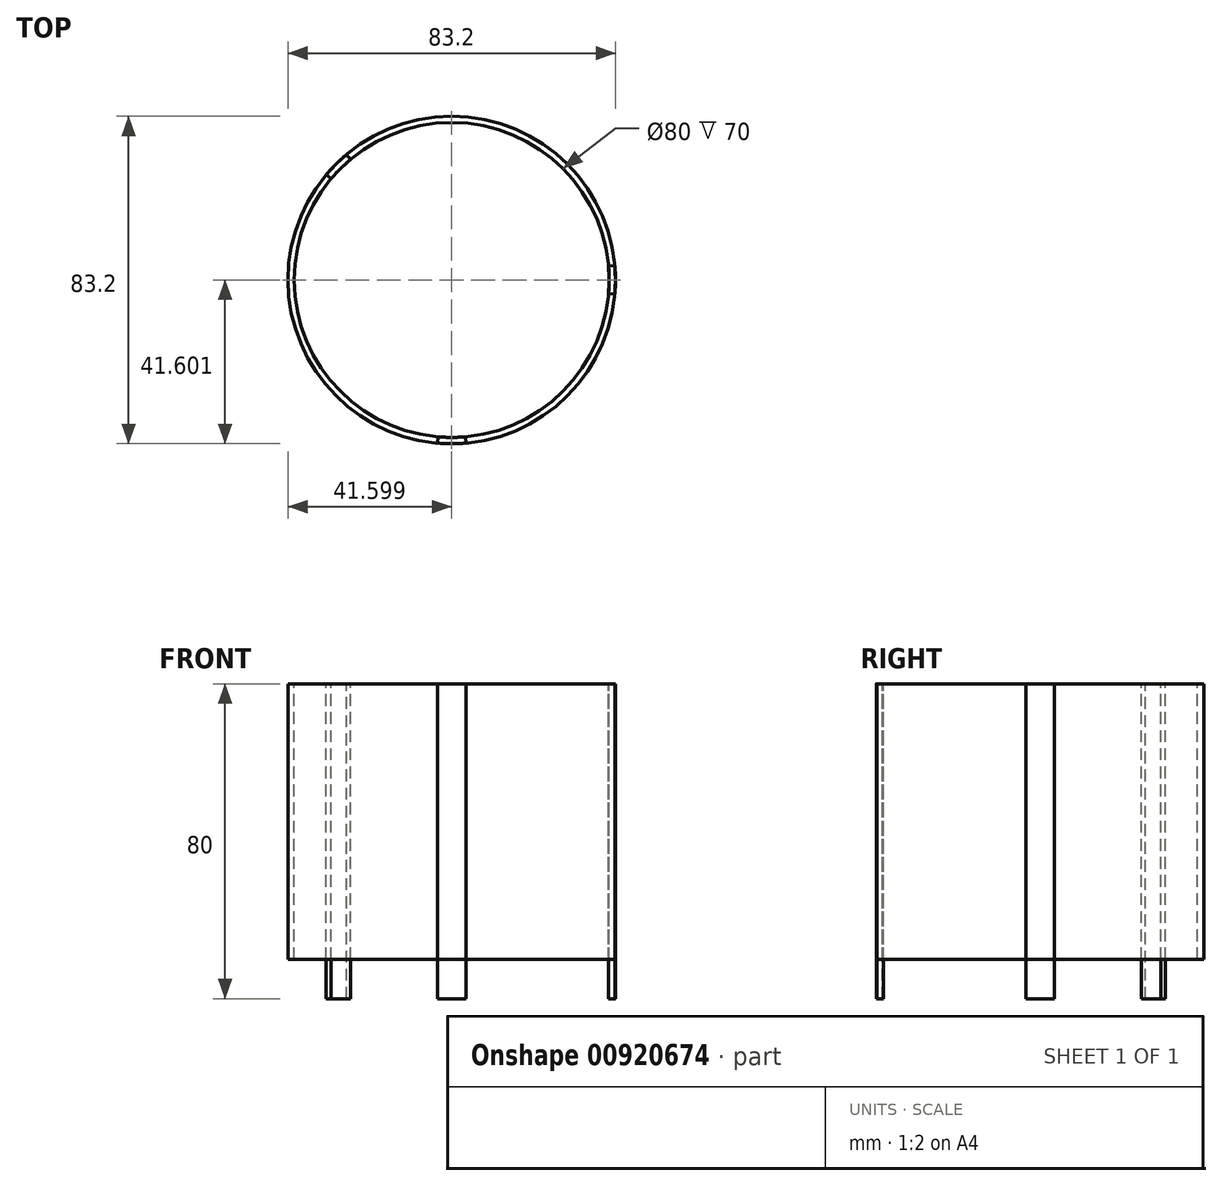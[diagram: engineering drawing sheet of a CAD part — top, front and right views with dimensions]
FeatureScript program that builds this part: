
annotation { "Feature Type Name" : "Feature", "Feature Type Description" : "" }
export const myFeature = defineFeature(function(context is Context, id is Id, definition is map)
    precondition{}
    {
        {
            var Q0;
            Q0=qCreatedBy(makeId("Top.planeOp"),FACE);
            var sketch = newSketch(context, id + "F0", { "sketchPlane" : qUnion([Q0])});
            skCircle(sketch, "E0", {"center": v(0, 0) * mm, "radius": 8 * mm});
            skLineSegment(sketch, "E1", {"start": v(0, 0) * mm, "end": v(-131.48, 0) * mm, "construction": true});
            skLineSegment(sketch, "E2", {"start": v(0, 0) * mm, "end": v(0, 113.56) * mm, "construction": true});
            skArc(sketch, "E3", {"start": v(-0.5, 107.5) * mm, "mid": v(-75.84, 76.2) * mm, "end": v(-107.5, 1) * mm});
            skLineSegment(sketch, "E4", {"start": v(-0.5, 7.98) * mm, "end": v(-0.5, 107.5) * mm});
            skLineSegment(sketch, "E5", {"start": v(-7.94, 1) * mm, "end": v(-107.5, 1) * mm});
            skArc(sketch, "E6", {"start": v(-107.5, 1) * mm, "mid": v(-107.5, 0.75) * mm, "end": v(-107.5, 0.5) * mm});
            skLineSegment(sketch, "E7", {"start": v(-7.94, 1) * mm, "end": v(-7.94, 1) * mm});
            skLineSegment(sketch, "E8.0", {"start": v(-7.98, 2.6) * mm, "end": v(-105.87, 2.6) * mm});
            skArc(sketch, "E8.1", {"start": v(-2.1, 105.88) * mm, "mid": v(-74.7, 75.06) * mm, "end": v(-105.87, 2.6) * mm});
            skLineSegment(sketch, "E8.2", {"start": v(-2.1, 12.6) * mm, "end": v(-2.1, 105.88) * mm});
            skCircle(sketch, "E9.0", {"center": v(0, 0) * mm, "radius": 9.6 * mm});
            skLineSegment(sketch, "E10", {"start": v(-101.02, 36.77) * mm, "end": v(-99.51, 36.22) * mm});
            skLineSegment(sketch, "E11", {"start": v(-90, 1) * mm, "end": v(-89.98, 2.61) * mm});
            skLineSegment(sketch, "E12", {"start": v(-30, 1) * mm, "end": v(-29.93, 2.6) * mm});
            skLineSegment(sketch, "E13", {"start": v(-2.1, 34.54) * mm, "end": v(-0.5, 34.66) * mm});
            skLineSegment(sketch, "E14", {"start": v(-2.1, 94.6) * mm, "end": v(-0.5, 94.63) * mm});
            skLineSegment(sketch, "E15", {"start": v(-36.77, 101.02) * mm, "end": v(-36.22, 99.51) * mm});
            skCircle(sketch, "E16", {"center": v(0, 0) * mm, "radius": 63.5 * mm, "construction": true});
            skLineSegment(sketch, "E17", {"start": v(0, 0) * mm, "end": v(-110.08, 110.08) * mm, "construction": true});
            skPoint(sketch, "E18", {"position": v(-44.9, 44.9) * mm});
            skCircle(sketch, "E19", {"center": v(-44.9, 44.9) * mm, "radius": 40 * mm});
            skCircle(sketch, "E20.0", {"center": v(-44.9, 44.9) * mm, "radius": 41.6 * mm});
            skLineSegment(sketch, "E21", {"start": v(-44.9, 44.9) * mm, "end": v(11.75, 44.9) * mm, "construction": true});
            skLineSegment(sketch, "E22", {"start": v(-44.9, 44.9) * mm, "end": v(-44.9, -4.5) * mm, "construction": true});
            skPoint(sketch, "E23", {"position": v(-44.9, 7.46) * mm});
            skPoint(sketch, "E24", {"position": v(-2.84, 44.9) * mm});
            skLineSegment(sketch, "E25", {"start": v(-44.9, 44.9) * mm, "end": v(8.17, 49.54) * mm});
            skLineSegment(sketch, "E26", {"start": v(-44.9, 44.9) * mm, "end": v(8.58, 40.22) * mm});
            skLineSegment(sketch, "E27", {"start": v(-44.9, 44.9) * mm, "end": v(-76.58, 82.65) * mm});
            skLineSegment(sketch, "E28", {"start": v(-44.9, 44.9) * mm, "end": v(-83.94, 77.66) * mm});
            skLineSegment(sketch, "E29", {"start": v(-44.9, 44.9) * mm, "end": v(-49.03, -2.28) * mm});
            skLineSegment(sketch, "E30", {"start": v(-44.9, 44.9) * mm, "end": v(-41.06, 1) * mm});
            skSolve(sketch);
        }
        {
            var Q0;
            {var subQ0=sQuery(id+"F0.wireOp",EDGE,"E27");var subQ1=sQuery(id+"F0.wireOp",EDGE,"E19");var subQ2=makeQuery(id+"F0.imprint","INTERSECT",VERTEX,{"derivedFrom":[subQ1,subQ0]});Q0=makeQuery(id+"F0.imprint","IMPRINT",FACE,{"disambiguationData":[TD([[makeQuery(id+"F0.imprint","IMPRINT",EDGE,{"disambiguationData":[TD([[subQ2,-1.0]])],"derivedFrom":subQ1}),-1.0]])]});}
            var Q1;
            {var subQ0=sQuery(id+"F0.wireOp",EDGE,"E25");var subQ1=sQuery(id+"F0.wireOp",EDGE,"E19");var subQ2=makeQuery(id+"F0.imprint","INTERSECT",VERTEX,{"derivedFrom":[subQ1,subQ0]});Q1=makeQuery(id+"F0.imprint","IMPRINT",FACE,{"disambiguationData":[TD([[makeQuery(id+"F0.imprint","IMPRINT",EDGE,{"disambiguationData":[TD([[subQ2,1.0]])],"derivedFrom":subQ1}),-1.0]])]});}
            var Q2;
            {var subQ0=sQuery(id+"F0.wireOp",EDGE,"E29");var subQ1=sQuery(id+"F0.wireOp",EDGE,"E19");var subQ2=makeQuery(id+"F0.imprint","INTERSECT",VERTEX,{"derivedFrom":[subQ1,subQ0]});Q2=makeQuery(id+"F0.imprint","IMPRINT",FACE,{"disambiguationData":[TD([[makeQuery(id+"F0.imprint","IMPRINT",EDGE,{"disambiguationData":[TD([[subQ2,-1.0]])],"derivedFrom":subQ1}),-1.0]])]});}
            extrude(context, id + "F1", {"entities" : qUnion([Q0, Q1, Q2]), "oppositeDirection" : true, "depth" : 80 * mm, "offsetDistance" : 25 * mm});
        }
        {
            var Q0;
            Q0=makeQuery(id+"F0.imprint","IMPRINT",FACE,{"disambiguationData":[TD([[makeQuery(id+"F0.imprint","IMPRINT",EDGE,{"derivedFrom":sQuery(id+"F0.wireOp",EDGE,"E19")}),-1.0]])]});
            extrude(context, id + "F2", {"entities" : qUnion([Q0]), "oppositeDirection" : true, "depth" : 70 * mm, "offsetDistance" : 25 * mm});
        }
    });
